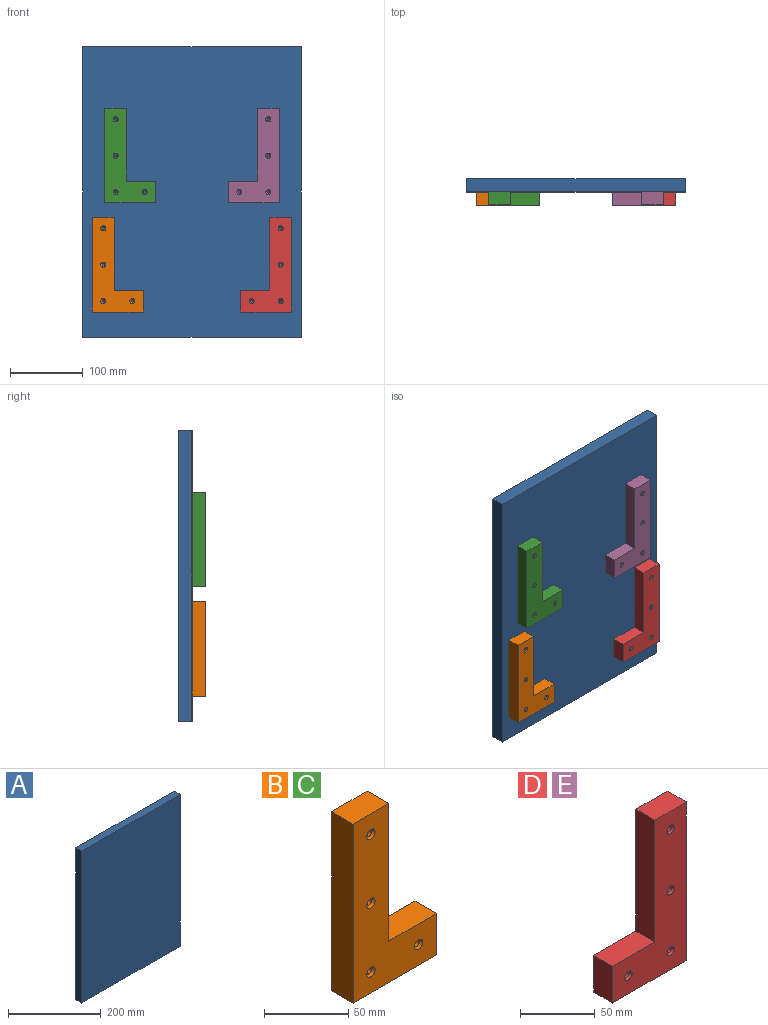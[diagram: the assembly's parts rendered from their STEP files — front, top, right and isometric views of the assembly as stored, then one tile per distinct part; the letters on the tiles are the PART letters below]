
ASSEMBLY  parts=5 mates=4
PART A: 10 faces, bbox 300x18x400 mm
  f0: plane 400x18mm, normal (-1,0,0), area 7200mm2, adj f1,f3,f4,f5
  f1: plane 300x18mm, normal (0,0,-1), area 5400mm2, adj f0,f2,f4,f5
  f2: plane 400x18mm, normal (1,0,0), area 7200mm2, adj f1,f3,f4,f5
  f3: plane 300x18mm, normal (0,0,1), area 5400mm2, adj f0,f2,f4,f5
  f4: plane 400x300mm, normal (0,-1,0), area 119987.4mm2, adj f0,f1,f2,f3,f6,f7,f8,f9
  f5: plane 400x300mm, normal (0,1,0), area 119987.4mm2, adj f0,f1,f2,f3,f6,f7,f8,f9
  f6: cylinder r=1mm len=18mm, axis (0,-1,0), area 113.1mm2, adj f4,f5
  f7: cylinder r=1mm len=18mm, axis (0,-1,0), area 113.1mm2, adj f4,f5
  f8: cylinder r=1mm len=18mm, axis (0,-1,0), area 113.1mm2, adj f4,f5
  f9: cylinder r=1mm len=18mm, axis (0,-1,0), area 113.1mm2, adj f4,f5
PART B: 16 faces, bbox 70x18x130 mm
  f0: plane 100x18mm, normal (1,0,0), area 1800mm2, adj f1,f5,f6,f7
  f1: plane 30x18mm, normal (0,0,1), area 540mm2, adj f0,f2,f6,f7
  f2: plane 130x18mm, normal (-1,0,0), area 2340mm2, adj f1,f3,f6,f7
  f3: plane 70x18mm, normal (0,0,-1), area 1260mm2, adj f2,f4,f6,f7
  f4: plane 30x18mm, normal (1,0,0), area 540mm2, adj f3,f5,f6,f7
  f5: plane 40x18mm, normal (0,0,1), area 720mm2, adj f0,f4,f6,f7
  f6: plane 130x70mm, normal (0,-1,0), area 4946.1mm2, adj f0,f1,f2,f3,f4,f5,f9,f11
  f7: plane 130x70mm, normal (0,1,0), area 5049.7mm2, adj f0,f1,f2,f3,f4,f5,f8,f10
  f8: cylinder r=2mm len=16.5mm, axis (0,-1,0), area 207.3mm2, adj f7,f9
  f9: cone r=2mm half-angle=45deg, axis (0,-1,0), area 36.7mm2, adj f6,f8
  f10: cylinder r=2mm len=16.5mm, axis (0,-1,0), area 207.3mm2, adj f7,f11
  f11: cone r=2mm half-angle=45deg, axis (0,-1,0), area 36.7mm2, adj f6,f10
  f12: cylinder r=2mm len=16.5mm, axis (0,-1,0), area 207.3mm2, adj f7,f13
  f13: cone r=2mm half-angle=45deg, axis (0,-1,0), area 36.7mm2, adj f6,f12
  f14: cylinder r=2mm len=16.5mm, axis (0,-1,0), area 207.3mm2, adj f7,f15
  f15: cone r=2mm half-angle=45deg, axis (0,-1,0), area 36.7mm2, adj f6,f14
PART C: same geometry as B
PART D: 16 faces, bbox 70x18x130 mm
  f0: plane 100x18mm, normal (-1,0,0), area 1800mm2, adj f1,f5,f6,f7
  f1: plane 30x18mm, normal (0,0,1), area 540mm2, adj f0,f2,f6,f7
  f2: plane 130x18mm, normal (1,0,0), area 2340mm2, adj f1,f3,f6,f7
  f3: plane 70x18mm, normal (0,0,-1), area 1260mm2, adj f2,f4,f6,f7
  f4: plane 30x18mm, normal (-1,0,0), area 540mm2, adj f3,f5,f6,f7
  f5: plane 40x18mm, normal (0,0,1), area 720mm2, adj f0,f4,f6,f7
  f6: plane 130x70mm, normal (0,-1,0), area 4946.1mm2, adj f0,f1,f2,f3,f4,f5,f9,f11
  f7: plane 130x70mm, normal (0,1,0), area 5049.7mm2, adj f0,f1,f2,f3,f4,f5,f8,f10
  f8: cylinder r=2mm len=16.5mm, axis (0,-1,0), area 207.3mm2, adj f7,f9
  f9: cone r=2mm half-angle=45deg, axis (0,-1,0), area 36.7mm2, adj f6,f8
  f10: cylinder r=2mm len=16.5mm, axis (0,-1,0), area 207.3mm2, adj f7,f11
  f11: cone r=2mm half-angle=45deg, axis (0,-1,0), area 36.7mm2, adj f6,f10
  f12: cylinder r=2mm len=16.5mm, axis (0,-1,0), area 207.3mm2, adj f7,f13
  f13: cone r=2mm half-angle=45deg, axis (0,-1,0), area 36.7mm2, adj f6,f12
  f14: cylinder r=2mm len=16.5mm, axis (0,-1,0), area 207.3mm2, adj f7,f15
  f15: cone r=2mm half-angle=45deg, axis (0,-1,0), area 36.7mm2, adj f6,f14
PART E: same geometry as D
PLACE A t=(-15.65,223.08,-113.58)mm
PLACE B t=(127.35,205.08,-78.58)mm
PLACE C t=(144.35,205.08,71.42)mm
PLACE D t=(141.35,205.08,-78.58)mm
PLACE E t=(124.35,205.08,71.42)mm
MATE fastened D.f10 <-> A.f9  axis (0,1,0) through (256.35,205.08,-63.58)mm
MATE fastened A.f8 <-> B.f10  axis (0,-1,0) through (12.35,205.08,-63.58)mm
MATE fastened A.f7 <-> E.f10  axis (0,-1,0) through (239.35,205.08,86.42)mm
MATE fastened C.f10 <-> A.f6  axis (0,1,0) through (29.35,205.08,86.42)mm
